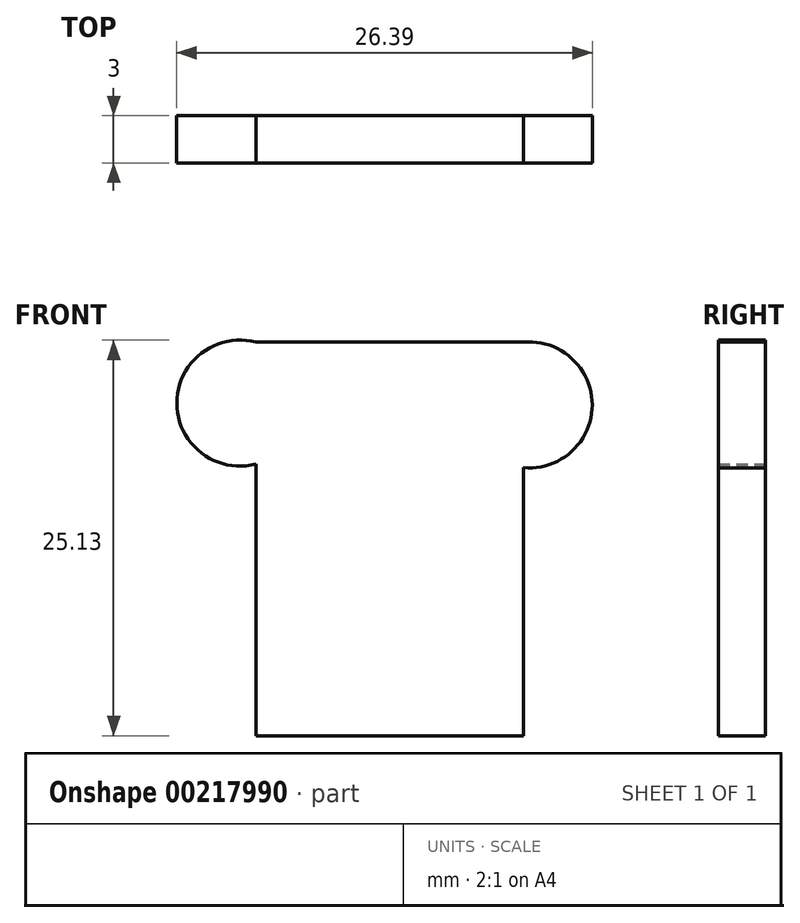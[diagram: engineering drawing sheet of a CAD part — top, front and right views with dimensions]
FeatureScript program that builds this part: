
annotation { "Feature Type Name" : "Feature", "Feature Type Description" : "" }
export const myFeature = defineFeature(function(context is Context, id is Id, definition is map)
    precondition{}
    {
        {
            var Q0;
            Q0=qCreatedBy(makeId("Front.planeOp"),FACE);
            var sketch = newSketch(context, id + "F0", { "sketchPlane" : qUnion([Q0])});
            skLineSegment(sketch, "E0", {"start": v(-2.9, 11.27) * mm, "end": v(-2.9, -6) * mm});
            skLineSegment(sketch, "E1", {"start": v(-2.9, -6) * mm, "end": v(14.1, -6) * mm});
            skLineSegment(sketch, "E2", {"start": v(14.1, -6) * mm, "end": v(14.1, 11.04) * mm});
            skArc(sketch, "E3", {"start": v(14.1, 11.04) * mm, "mid": v(18.47, 15.02) * mm, "end": v(14.1, 19) * mm});
            skLineSegment(sketch, "E4", {"start": v(-2.9, 19) * mm, "end": v(14.1, 19) * mm});
            skArc(sketch, "E5", {"start": v(-2.9, 19) * mm, "mid": v(-7.92, 15.14) * mm, "end": v(-2.9, 11.27) * mm});
            skSolve(sketch);
        }
        {
            var Q0;
            Q0=qSketchRegion(id+"F0",true);
            extrude(context, id + "F1", {"entities" : qUnion([Q0]), "depth" : 3 * mm});
        }
    });
